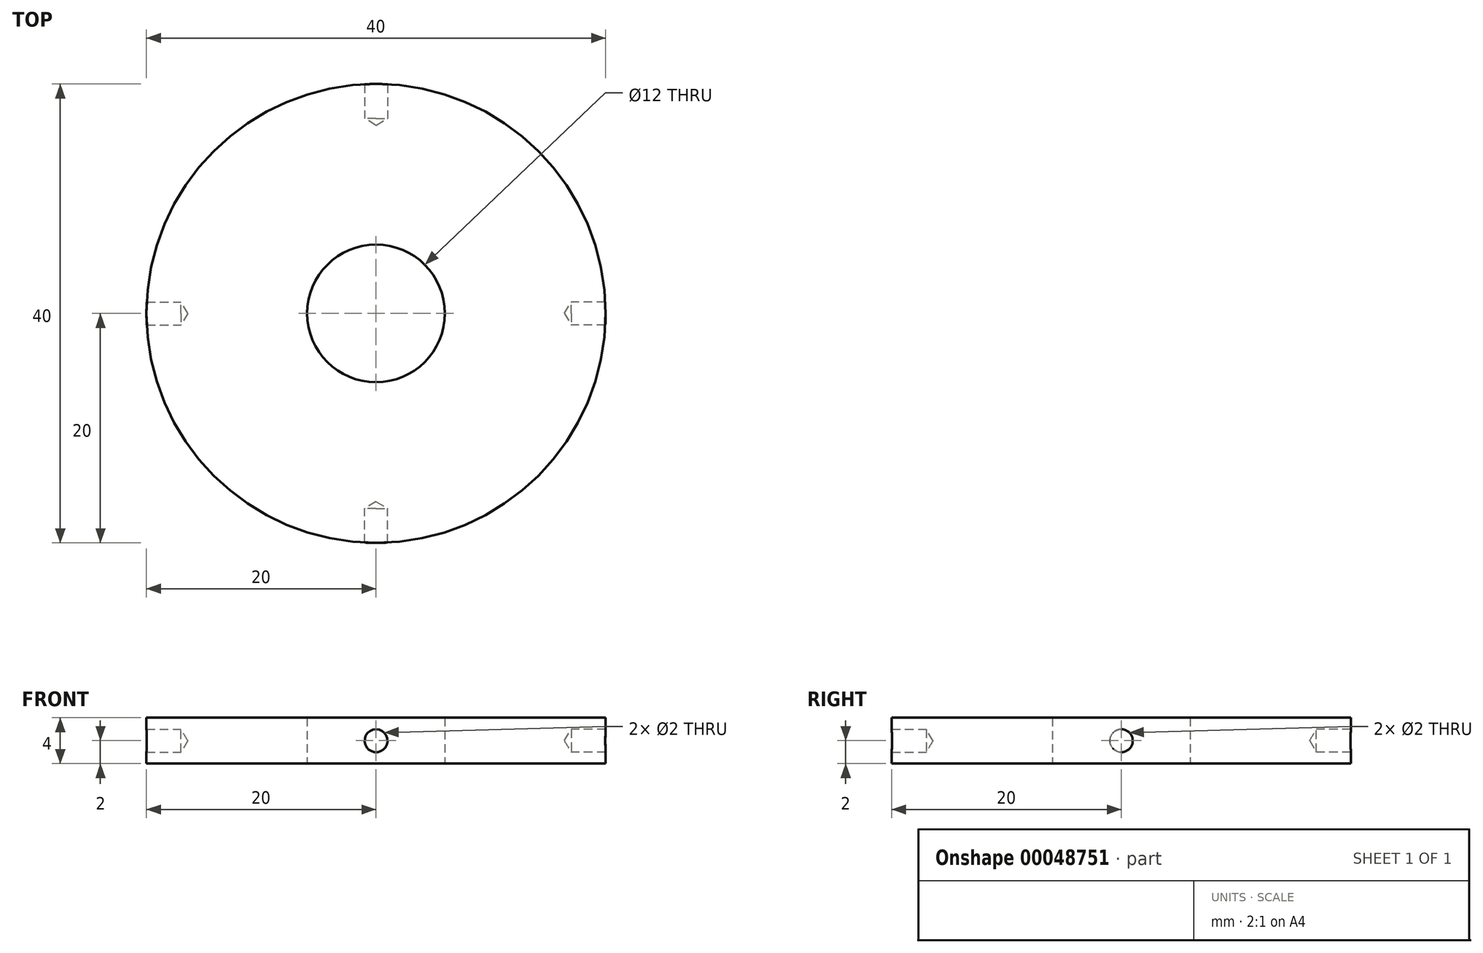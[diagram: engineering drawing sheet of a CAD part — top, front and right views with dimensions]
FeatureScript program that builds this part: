
annotation { "Feature Type Name" : "Feature", "Feature Type Description" : "" }
export const myFeature = defineFeature(function(context is Context, id is Id, definition is map)
    precondition{}
    {
        {
            var Q0;
            Q0=qCreatedBy(makeId("Top.planeOp"),FACE);
            var sketch = newSketch(context, id + "F0", { "sketchPlane" : qUnion([Q0])});
            skCircle(sketch, "E0", {"center": v(0, 0) * mm, "radius": 6 * mm});
            skCircle(sketch, "E1", {"center": v(0, 0) * mm, "radius": 20 * mm});
            skSolve(sketch);
        }
        {
            var Q0;
            Q0=makeQuery(id+"F0.imprint","IMPRINT",FACE,{"disambiguationData":[TD([[makeQuery(id+"F0.imprint","IMPRINT",EDGE,{"derivedFrom":sQuery(id+"F0.wireOp",EDGE,"E0")}),-1.0]])]});
            extrude(context, id + "F1", {"entities" : qUnion([Q0]), "depth" : 4 * mm, "symmetric" : true});
        }
        {
            var Q0;
            Q0=qCreatedBy(makeId("Right.planeOp"),FACE);
            cPlane(context, id + "F2", {"entities" : qUnion([Q0]), "cplaneType" : CPlaneType.OFFSET, "offset" : 20 * mm, "width" : 150 * mm, "height" : 150 * mm});
        }
        {
            var Q0;
            Q0=qCreatedBy(id+"F2.planeOp",FACE);
            var sketch = newSketch(context, id + "F3", { "sketchPlane" : qUnion([Q0])});
            skPoint(sketch, "E2", {"position": v(0, 0) * mm});
            skSolve(sketch);
        }
        {
            var Q0;
            Q0=sQuery(id+"F3.wireOp",VERTEX,"E2");
            var Q1;
            Q1=makeQuery(id+"F1.opExtrude","SWEPT_BODY",BODY,{"disambiguationData":[OSD([sQuery(id+"F0.wireOp",EDGE,"E0"),sQuery(id+"F0.wireOp",EDGE,"E1")])]});
            hole(context, id + "F4", {"style" : HoleStyle.SIMPLE, "endStyle" : HoleEndStyle.BLIND, "holeDiameter" : 2 * mm, "holeDepth" : 3 * mm, "tappedDepth" : 12 * mm, "tapClearance" : 3, "locations" : qUnion([Q0]), "scope" : qUnion([Q1]), "startStyle" : HoleStartStyle.SKETCH});
        }
        {
            var Q0;
            Q0=qCreatedBy(makeId("Right.planeOp"),FACE);
            cPlane(context, id + "F5", {"entities" : qUnion([Q0]), "cplaneType" : CPlaneType.OFFSET, "offset" : 20 * mm, "oppositeDirection" : true, "width" : 150 * mm, "height" : 150 * mm});
        }
        {
            var Q0;
            Q0=qCreatedBy(id+"F5.planeOp",FACE);
            var sketch = newSketch(context, id + "F6", { "sketchPlane" : qUnion([Q0])});
            skPoint(sketch, "E3", {"position": v(0, 0) * mm});
            skSolve(sketch);
        }
        {
            var Q0;
            Q0=sQuery(id+"F6.wireOp",VERTEX,"E3");
            var Q1;
            Q1=makeQuery(id+"F1.opExtrude","SWEPT_BODY",BODY,{"disambiguationData":[OSD([sQuery(id+"F0.wireOp",EDGE,"E0"),sQuery(id+"F0.wireOp",EDGE,"E1")])]});
            hole(context, id + "F7", {"style" : HoleStyle.SIMPLE, "endStyle" : HoleEndStyle.BLIND, "oppositeDirection" : true, "holeDiameter" : 2 * mm, "holeDepth" : 3 * mm, "tappedDepth" : 12 * mm, "tapClearance" : 3, "locations" : qUnion([Q0]), "scope" : qUnion([Q1]), "startStyle" : HoleStartStyle.SKETCH});
        }
        {
            var Q0;
            Q0=qCreatedBy(makeId("Front.planeOp"),FACE);
            cPlane(context, id + "F8", {"entities" : qUnion([Q0]), "cplaneType" : CPlaneType.OFFSET, "offset" : 20 * mm, "width" : 150 * mm, "height" : 150 * mm});
        }
        {
            var Q0;
            Q0=qCreatedBy(id+"F8.planeOp",FACE);
            var sketch = newSketch(context, id + "F9", { "sketchPlane" : qUnion([Q0])});
            skPoint(sketch, "E4", {"position": v(0, 0) * mm});
            skSolve(sketch);
        }
        {
            var Q0;
            Q0=sQuery(id+"F9.wireOp",VERTEX,"E4");
            var Q1;
            Q1=makeQuery(id+"F1.opExtrude","SWEPT_BODY",BODY,{"disambiguationData":[OSD([sQuery(id+"F0.wireOp",EDGE,"E0"),sQuery(id+"F0.wireOp",EDGE,"E1")])]});
            hole(context, id + "F10", {"style" : HoleStyle.SIMPLE, "endStyle" : HoleEndStyle.BLIND, "holeDiameter" : 2 * mm, "holeDepth" : 3 * mm, "tappedDepth" : 12 * mm, "tapClearance" : 3, "locations" : qUnion([Q0]), "scope" : qUnion([Q1]), "startStyle" : HoleStartStyle.SKETCH});
        }
        {
            var Q0;
            Q0=qCreatedBy(makeId("Front.planeOp"),FACE);
            cPlane(context, id + "F11", {"entities" : qUnion([Q0]), "cplaneType" : CPlaneType.OFFSET, "offset" : 20 * mm, "oppositeDirection" : true, "width" : 150 * mm, "height" : 150 * mm});
        }
        {
            var Q0;
            Q0=qCreatedBy(id+"F11.planeOp",FACE);
            var sketch = newSketch(context, id + "F12", { "sketchPlane" : qUnion([Q0])});
            skPoint(sketch, "E5", {"position": v(0, 0) * mm});
            skSolve(sketch);
        }
        {
            var Q0;
            Q0=sQuery(id+"F12.wireOp",VERTEX,"E5");
            var Q1;
            Q1=makeQuery(id+"F1.opExtrude","SWEPT_BODY",BODY,{"disambiguationData":[OSD([sQuery(id+"F0.wireOp",EDGE,"E0"),sQuery(id+"F0.wireOp",EDGE,"E1")])]});
            hole(context, id + "F13", {"style" : HoleStyle.SIMPLE, "endStyle" : HoleEndStyle.BLIND, "oppositeDirection" : true, "holeDiameter" : 2 * mm, "holeDepth" : 3 * mm, "tappedDepth" : 12 * mm, "tapClearance" : 3, "locations" : qUnion([Q0]), "scope" : qUnion([Q1]), "startStyle" : HoleStartStyle.SKETCH});
        }
    });
